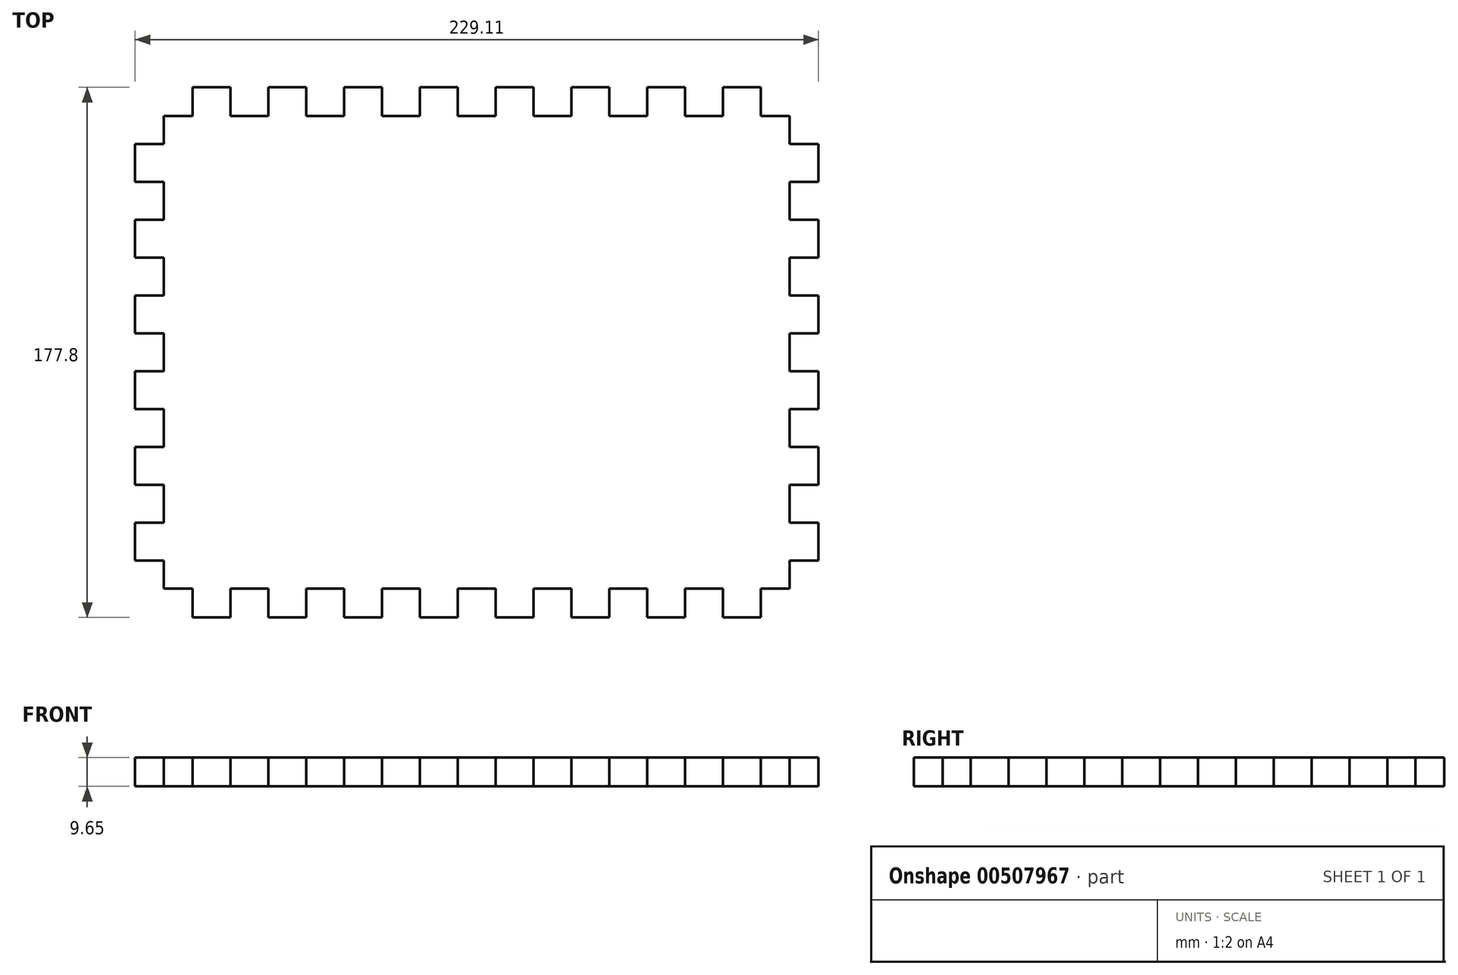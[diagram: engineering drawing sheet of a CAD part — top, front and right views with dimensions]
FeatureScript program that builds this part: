
annotation { "Feature Type Name" : "Feature", "Feature Type Description" : "" }
export const myFeature = defineFeature(function(context is Context, id is Id, definition is map)
    precondition{}
    {
        {
            var Q0;
            Q0=qCreatedBy(makeId("Top.planeOp"),FACE);
            var sketch = newSketch(context, id + "F0", { "sketchPlane" : qUnion([Q0])});
            skLineSegment(sketch, "E0.bottom", {"start": v(19.3, 0) * mm, "end": v(32, 0) * mm});
            skLineSegment(sketch, "E0.top", {"start": v(19.3, -177.8) * mm, "end": v(19.3, -177.8) * mm});
            skLineSegment(sketch, "E0.left", {"start": v(0, -19.05) * mm, "end": v(0, -31.75) * mm});
            skLineSegment(sketch, "E1", {"start": v(0, -19.05) * mm, "end": v(9.65, -19.05) * mm});
            skLineSegment(sketch, "E2", {"start": v(9.65, -19.05) * mm, "end": v(9.65, -9.65) * mm});
            skLineSegment(sketch, "E3", {"start": v(9.65, -9.65) * mm, "end": v(19.3, -9.65) * mm});
            skLineSegment(sketch, "E4", {"start": v(19.3, -9.65) * mm, "end": v(19.3, 0) * mm});
            skPoint(sketch, "E5.orphan", {"position": v(0, 0) * mm});
            skLineSegment(sketch, "E6", {"start": v(32, 0) * mm, "end": v(32, -9.65) * mm});
            skLineSegment(sketch, "E7", {"start": v(32, -9.65) * mm, "end": v(44.7, -9.65) * mm});
            skLineSegment(sketch, "E8", {"start": v(44.7, -9.65) * mm, "end": v(44.7, 0) * mm});
            skLineSegment(sketch, "E9", {"start": v(44.7, 0) * mm, "end": v(57.4, 0) * mm});
            skLineSegment(sketch, "E10", {"start": v(57.4, 0) * mm, "end": v(57.4, -9.65) * mm});
            skLineSegment(sketch, "E11", {"start": v(57.4, -9.65) * mm, "end": v(70.1, -9.65) * mm});
            skLineSegment(sketch, "E12", {"start": v(70.1, -9.65) * mm, "end": v(70.1, 0) * mm});
            skLineSegment(sketch, "E13", {"start": v(70.1, 0) * mm, "end": v(82.8, 0) * mm});
            skLineSegment(sketch, "E14", {"start": v(82.8, 0) * mm, "end": v(82.8, -9.65) * mm});
            skLineSegment(sketch, "E15", {"start": v(82.8, -9.65) * mm, "end": v(95.5, -9.65) * mm});
            skLineSegment(sketch, "E16", {"start": v(95.5, -9.65) * mm, "end": v(95.5, 0) * mm});
            skLineSegment(sketch, "E17", {"start": v(95.5, 0) * mm, "end": v(108.2, 0) * mm});
            skLineSegment(sketch, "E18", {"start": v(108.2, 0) * mm, "end": v(108.2, -9.65) * mm});
            skLineSegment(sketch, "E19", {"start": v(108.2, -9.65) * mm, "end": v(120.9, -9.65) * mm});
            skLineSegment(sketch, "E20", {"start": v(120.9, -9.65) * mm, "end": v(120.9, 0) * mm});
            skLineSegment(sketch, "E21.trimOffspring", {"start": v(120.9, 0) * mm, "end": v(133.6, 0) * mm});
            skLineSegment(sketch, "E22", {"start": v(133.6, 0) * mm, "end": v(133.6, -9.65) * mm});
            skLineSegment(sketch, "E23", {"start": v(133.6, -9.65) * mm, "end": v(146.3, -9.65) * mm});
            skLineSegment(sketch, "E24", {"start": v(146.3, -9.65) * mm, "end": v(146.3, 0) * mm});
            skLineSegment(sketch, "E25", {"start": v(146.3, 0) * mm, "end": v(159, 0) * mm});
            skLineSegment(sketch, "E26", {"start": v(159, 0) * mm, "end": v(159, -9.65) * mm});
            skLineSegment(sketch, "E27", {"start": v(159, -9.65) * mm, "end": v(171.7, -9.65) * mm});
            skLineSegment(sketch, "E28", {"start": v(171.7, -9.65) * mm, "end": v(171.7, 0) * mm});
            skLineSegment(sketch, "E29", {"start": v(171.7, 0) * mm, "end": v(184.4, 0) * mm});
            skLineSegment(sketch, "E30", {"start": v(184.4, 0) * mm, "end": v(184.4, -9.65) * mm});
            skLineSegment(sketch, "E31", {"start": v(184.4, -9.65) * mm, "end": v(197.1, -9.65) * mm});
            skLineSegment(sketch, "E32", {"start": v(197.1, -9.65) * mm, "end": v(197.1, 0) * mm});
            skLineSegment(sketch, "E33.trimOffspring", {"start": v(197.1, 0) * mm, "end": v(209.8, 0) * mm});
            skLineSegment(sketch, "E34", {"start": v(209.8, 0) * mm, "end": v(209.8, -9.65) * mm});
            skLineSegment(sketch, "E35", {"start": v(209.8, -9.65) * mm, "end": v(219.46, -9.65) * mm});
            skLineSegment(sketch, "E36", {"start": v(219.46, -9.65) * mm, "end": v(219.46, -19.05) * mm});
            skLineSegment(sketch, "E37", {"start": v(219.46, -19.05) * mm, "end": v(229.1, -19.05) * mm});
            skPoint(sketch, "E38.orphan", {"position": v(228.6, 0) * mm});
            skLineSegment(sketch, "E39", {"start": v(0, -31.75) * mm, "end": v(9.65, -31.75) * mm});
            skLineSegment(sketch, "E40", {"start": v(9.65, -31.75) * mm, "end": v(9.65, -44.45) * mm});
            skLineSegment(sketch, "E41", {"start": v(9.65, -44.45) * mm, "end": v(0, -44.45) * mm});
            skLineSegment(sketch, "E42", {"start": v(0, -44.45) * mm, "end": v(0, -57.15) * mm});
            skLineSegment(sketch, "E43", {"start": v(0, -57.15) * mm, "end": v(9.65, -57.15) * mm});
            skLineSegment(sketch, "E44", {"start": v(9.65, -57.15) * mm, "end": v(9.65, -69.85) * mm});
            skLineSegment(sketch, "E45", {"start": v(9.65, -69.85) * mm, "end": v(0, -69.85) * mm});
            skLineSegment(sketch, "E46", {"start": v(0, -69.85) * mm, "end": v(0, -82.55) * mm});
            skLineSegment(sketch, "E47", {"start": v(0, -82.55) * mm, "end": v(9.65, -82.55) * mm});
            skLineSegment(sketch, "E48", {"start": v(9.65, -82.55) * mm, "end": v(9.65, -95.25) * mm});
            skLineSegment(sketch, "E49", {"start": v(9.65, -95.25) * mm, "end": v(0, -95.25) * mm});
            skLineSegment(sketch, "E50", {"start": v(0, -95.25) * mm, "end": v(0, -107.95) * mm});
            skLineSegment(sketch, "E51", {"start": v(0, -107.95) * mm, "end": v(9.65, -107.95) * mm});
            skLineSegment(sketch, "E52", {"start": v(9.65, -107.95) * mm, "end": v(9.65, -120.65) * mm});
            skLineSegment(sketch, "E53", {"start": v(9.65, -120.65) * mm, "end": v(0, -120.65) * mm});
            skLineSegment(sketch, "E54", {"start": v(0, -120.65) * mm, "end": v(0, -133.35) * mm});
            skLineSegment(sketch, "E55", {"start": v(0, -133.35) * mm, "end": v(9.65, -133.35) * mm});
            skLineSegment(sketch, "E56", {"start": v(9.65, -133.35) * mm, "end": v(9.65, -146.05) * mm});
            skLineSegment(sketch, "E57", {"start": v(9.65, -146.05) * mm, "end": v(0, -146.05) * mm});
            skLineSegment(sketch, "E58", {"start": v(0, -146.05) * mm, "end": v(0, -158.75) * mm});
            skLineSegment(sketch, "E59", {"start": v(0, -158.75) * mm, "end": v(9.65, -158.75) * mm});
            skLineSegment(sketch, "E60", {"start": v(9.65, -158.75) * mm, "end": v(9.65, -168.15) * mm});
            skLineSegment(sketch, "E61", {"start": v(9.65, -168.15) * mm, "end": v(19.3, -168.15) * mm});
            skLineSegment(sketch, "E62", {"start": v(19.3, -168.15) * mm, "end": v(19.3, -177.8) * mm});
            skLineSegment(sketch, "E63", {"start": v(0, 0) * mm, "end": v(0, -19.05) * mm, "construction": true});
            skLineSegment(sketch, "E64", {"start": v(0, 0) * mm, "end": v(19.3, 0) * mm, "construction": true});
            skLineSegment(sketch, "E65", {"start": v(9.65, -88.9) * mm, "end": v(114.82, -88.9) * mm, "construction": true});
            skPoint(sketch, "E65.endSnap0", {"position": v(9.65, -88.9) * mm});
            skLineSegment(sketch, "E66.MirrorCS", {"start": v(0, 0) * mm, "end": v(0, 19.05) * mm, "construction": true});
            skLineSegment(sketch, "E67.MirrorCS", {"start": v(9.65, 88.9) * mm, "end": v(114.82, 88.9) * mm, "construction": true});
            skLineSegment(sketch, "E68.MirrorCS", {"start": v(19.3, -177.8) * mm, "end": v(32, -177.8) * mm});
            skLineSegment(sketch, "E69.MirrorCS", {"start": v(32, -177.8) * mm, "end": v(32, -168.15) * mm});
            skLineSegment(sketch, "E70.MirrorCS", {"start": v(32, -168.15) * mm, "end": v(44.7, -168.15) * mm});
            skLineSegment(sketch, "E71.MirrorCS", {"start": v(44.7, -168.15) * mm, "end": v(44.7, -177.8) * mm});
            skLineSegment(sketch, "E72.MirrorCS", {"start": v(44.7, -177.8) * mm, "end": v(57.4, -177.8) * mm});
            skLineSegment(sketch, "E73.MirrorCS", {"start": v(57.4, -177.8) * mm, "end": v(57.4, -168.15) * mm});
            skLineSegment(sketch, "E74.MirrorCS", {"start": v(57.4, -168.15) * mm, "end": v(70.1, -168.15) * mm});
            skLineSegment(sketch, "E75.MirrorCS", {"start": v(70.1, -168.15) * mm, "end": v(70.1, -177.8) * mm});
            skLineSegment(sketch, "E76.MirrorCS", {"start": v(70.1, -177.8) * mm, "end": v(82.8, -177.8) * mm});
            skLineSegment(sketch, "E77.MirrorCS", {"start": v(82.8, -177.8) * mm, "end": v(82.8, -168.15) * mm});
            skLineSegment(sketch, "E78.MirrorCS", {"start": v(82.8, -168.15) * mm, "end": v(95.5, -168.15) * mm});
            skLineSegment(sketch, "E79.MirrorCS", {"start": v(95.5, -168.15) * mm, "end": v(95.5, -177.8) * mm});
            skLineSegment(sketch, "E80.MirrorCS", {"start": v(95.5, -177.8) * mm, "end": v(108.2, -177.8) * mm});
            skLineSegment(sketch, "E81.MirrorCS", {"start": v(108.2, -177.8) * mm, "end": v(108.2, -168.15) * mm});
            skLineSegment(sketch, "E82.MirrorCS", {"start": v(108.2, -168.15) * mm, "end": v(120.9, -168.15) * mm});
            skLineSegment(sketch, "E83.MirrorCS", {"start": v(120.9, -168.15) * mm, "end": v(120.9, -177.8) * mm});
            skLineSegment(sketch, "E84.MirrorCS", {"start": v(120.9, -177.8) * mm, "end": v(133.6, -177.8) * mm});
            skLineSegment(sketch, "E85.MirrorCS", {"start": v(133.6, -177.8) * mm, "end": v(133.6, -168.15) * mm});
            skLineSegment(sketch, "E86.MirrorCS", {"start": v(133.6, -168.15) * mm, "end": v(146.3, -168.15) * mm});
            skLineSegment(sketch, "E87.MirrorCS", {"start": v(146.3, -168.15) * mm, "end": v(146.3, -177.8) * mm});
            skLineSegment(sketch, "E88.MirrorCS", {"start": v(146.3, -177.8) * mm, "end": v(159, -177.8) * mm});
            skLineSegment(sketch, "E89.MirrorCS", {"start": v(159, -177.8) * mm, "end": v(159, -168.15) * mm});
            skLineSegment(sketch, "E90.MirrorCS", {"start": v(159, -168.15) * mm, "end": v(171.7, -168.15) * mm});
            skLineSegment(sketch, "E91.MirrorCS", {"start": v(171.7, -168.15) * mm, "end": v(171.7, -177.8) * mm});
            skLineSegment(sketch, "E92.MirrorCS", {"start": v(171.7, -177.8) * mm, "end": v(184.4, -177.8) * mm});
            skLineSegment(sketch, "E93.MirrorCS", {"start": v(184.4, -177.8) * mm, "end": v(184.4, -168.15) * mm});
            skLineSegment(sketch, "E94.MirrorCS", {"start": v(184.4, -168.15) * mm, "end": v(197.1, -168.15) * mm});
            skLineSegment(sketch, "E95.MirrorCS", {"start": v(197.1, -168.15) * mm, "end": v(197.1, -177.8) * mm});
            skLineSegment(sketch, "E96.MirrorCS", {"start": v(197.1, -177.8) * mm, "end": v(209.8, -177.8) * mm});
            skLineSegment(sketch, "E97.MirrorCS", {"start": v(209.8, -177.8) * mm, "end": v(209.8, -168.15) * mm});
            skLineSegment(sketch, "E98.MirrorCS", {"start": v(209.8, -168.15) * mm, "end": v(219.46, -168.15) * mm});
            skLineSegment(sketch, "E99.MirrorCS", {"start": v(219.46, -168.15) * mm, "end": v(219.46, -158.75) * mm});
            skLineSegment(sketch, "E100.MirrorCS", {"start": v(219.46, -158.75) * mm, "end": v(229.1, -158.75) * mm});
            skLineSegment(sketch, "E101", {"start": v(114.55, -9.65) * mm, "end": v(114.55, -60.36) * mm, "construction": true});
            skLineSegment(sketch, "E102.MirrorCS", {"start": v(219.46, -19.05) * mm, "end": v(219.46, -9.65) * mm});
            skLineSegment(sketch, "E103.MirrorCS", {"start": v(229.1, -19.05) * mm, "end": v(219.46, -19.05) * mm});
            skLineSegment(sketch, "E104.MirrorCS", {"start": v(229.1, -19.05) * mm, "end": v(229.1, -31.75) * mm});
            skLineSegment(sketch, "E105.MirrorCS", {"start": v(229.1, -31.75) * mm, "end": v(219.46, -31.75) * mm});
            skLineSegment(sketch, "E106.MirrorCS", {"start": v(219.46, -31.75) * mm, "end": v(219.46, -44.45) * mm});
            skLineSegment(sketch, "E107.MirrorCS", {"start": v(219.46, -44.45) * mm, "end": v(229.1, -44.45) * mm});
            skLineSegment(sketch, "E108.MirrorCS", {"start": v(229.1, -44.45) * mm, "end": v(229.1, -57.15) * mm});
            skLineSegment(sketch, "E109.MirrorCS", {"start": v(229.1, -57.15) * mm, "end": v(219.46, -57.15) * mm});
            skLineSegment(sketch, "E110.MirrorCS", {"start": v(219.46, -57.15) * mm, "end": v(219.46, -69.85) * mm});
            skLineSegment(sketch, "E111.MirrorCS", {"start": v(219.46, -69.85) * mm, "end": v(229.1, -69.85) * mm});
            skLineSegment(sketch, "E112.MirrorCS", {"start": v(229.1, -69.85) * mm, "end": v(229.1, -82.55) * mm});
            skLineSegment(sketch, "E113.MirrorCS", {"start": v(229.1, -82.55) * mm, "end": v(219.46, -82.55) * mm});
            skLineSegment(sketch, "E114.MirrorCS", {"start": v(219.46, -82.55) * mm, "end": v(219.46, -95.25) * mm});
            skLineSegment(sketch, "E115.MirrorCS", {"start": v(219.46, -95.25) * mm, "end": v(229.1, -95.25) * mm});
            skLineSegment(sketch, "E116.MirrorCS", {"start": v(229.1, -95.25) * mm, "end": v(229.1, -107.95) * mm});
            skLineSegment(sketch, "E117.MirrorCS", {"start": v(229.1, -107.95) * mm, "end": v(219.46, -107.95) * mm});
            skLineSegment(sketch, "E118.MirrorCS", {"start": v(219.46, -107.95) * mm, "end": v(219.46, -120.65) * mm});
            skLineSegment(sketch, "E119.MirrorCS", {"start": v(219.46, -120.65) * mm, "end": v(229.1, -120.65) * mm});
            skLineSegment(sketch, "E120.MirrorCS", {"start": v(229.1, -120.65) * mm, "end": v(229.1, -133.35) * mm});
            skLineSegment(sketch, "E121.MirrorCS", {"start": v(229.1, -133.35) * mm, "end": v(219.46, -133.35) * mm});
            skLineSegment(sketch, "E122.MirrorCS", {"start": v(219.46, -133.35) * mm, "end": v(219.46, -146.05) * mm});
            skLineSegment(sketch, "E123.MirrorCS", {"start": v(219.46, -146.05) * mm, "end": v(229.1, -146.05) * mm});
            skLineSegment(sketch, "E124.MirrorCS", {"start": v(229.1, -146.05) * mm, "end": v(229.1, -158.75) * mm});
            skSolve(sketch);
        }
        {
            var Q0;
            Q0=makeQuery(id+"F0.imprint","IMPRINT",FACE,{"disambiguationData":[TD([[makeQuery(id+"F0.imprint","IMPRINT",EDGE,{"derivedFrom":sQuery(id+"F0.wireOp",EDGE,"E1")}),-1.0]])]});
            extrude(context, id + "F1", {"entities" : qUnion([Q0]), "depth" : 9.65 * mm});
        }
    });
